# Revit family: RUSHWORK_ 6460
name_source: partatom
category: Арматура трубопроводов
units: mm (PartAtom-declared; Revit-internal decimal feet)

## family parameters
Всегда вертикально = Нет
На основе рабочей плоскости = Нет
Общий = Нет
При загрузке вырезать с полостями = Нет
Размер круглого соединителя = Использовать диаметр
Тип детали = Вставляется

## types (8) — shared parameters
ADSK_Единица измерения = шт
ADSK_Завод-изготовитель = ООО TД "РАШВОРК"
URL = https://rwru.ru
Изготовитель = ООО TД "РАШВОРК"
Корпус = нерж. сталь CF8M
zero-valued in all types: Отметка по умолчанию

## per-type parameters (varying)
| type | ADSK_Код изделия | ADSK_Масса | D1 | D2 | D3 | DN | H | H3 | H4 | H5 | L | L1 | L2 |
| Фильтр сетчатый РАШВОРК 6460-008-40, DN008 PN40, корпус - CF8М, сетка - AISI316, ячейка - 1 мм, ВР/ВР | 6460-008-40 | 0.2 | 26 мм | 24 мм | 27 мм | 10 мм | 43 мм | 25 мм | 21 мм | 7 мм | 64 мм | 10 мм | 16 мм |
| Фильтр сетчатый РАШВОРК 6460-010-40, DN010 PN40, корпус - CF8М, сетка - AISI316, ячейка - 1 мм, ВР/ВР | 6460-010-40 | 0.2 | 26 мм | 24 мм | 24 мм | 12 мм | 43 мм | 25 мм | 21 мм | 7 мм | 64 мм | 10 мм | 16 мм |
| Фильтр сетчатый РАШВОРК 6460-020-40, DN020 PN40, корпус - CF8М, сетка - AISI316, ячейка - 1 мм, ВР/ВР | 6460-020-40 | 0.33 | 32 мм | 29 мм | 29 мм | 20 мм | 50 мм | 32 мм | 21 мм | 7 мм | 80 мм | 16 мм | 15 мм |
| Фильтр сетчатый РАШВОРК 6460-015-40, DN015 PN40, корпус - CF8М, сетка - AISI316, ячейка - 1 мм, ВР/ВР | 6460-015-40 | 0.2 | 26 мм | 24 мм | 24 мм | 15 мм | 43 мм | 25 мм | 21 мм | 7 мм | 64 мм | 10 мм | 16 мм |
| Фильтр сетчатый РАШВОРК 6460-025-40, DN025 PN40, корпус - CF8М, сетка - AISI316, ячейка - 1 мм, ВР/ВР | 6460-025-40 | 0.58 | 40 мм | 34 мм | 45 мм | 25 мм | 65 мм | 43 мм | 25 мм | 9 мм | 90 мм | 16 мм | 16 мм |
| Фильтр сетчатый РАШВОРК 6460-032-40, DN032 PN40, корпус - CF8М, сетка - AISI316, ячейка - 1 мм, ВР/ВР | 6460-032-40 | 0.75 | 48 мм | 45 мм | 47 мм | 32 мм | 69 мм | 47 мм | 25 мм | 10 мм | 106 мм | 20 мм | 16 мм |
| Фильтр сетчатый РАШВОРК 6460-040-40, DN040 PN40, корпус - CF8М, сетка - AISI316, ячейка - 1 мм, ВР/ВР | 6460-040-40 | 1.05 | 55 мм | 51 мм | 55 мм | 40 мм | 79 мм | 53 мм | 27 мм | 11 мм | 119 мм | 22 мм | 16 мм |
| Фильтр сетчатый РАШВОРК 6460-050-40, DN050 PN40, корпус - CF8М, сетка - AISI316, ячейка - 1 мм, ВР/ВР | 6460-050-40 | 1.57 | 68 мм | 65 мм | 67 мм | 50 мм | 92 мм | 66 мм | 29 мм | 12 мм | 140 мм | 22 мм | 29 мм |

note: column(s) folded — value = type name in every type: ADSK_Наименование

## geometry (parser evidence)
native form markers: Blend x21
no freeform markers — native parametric forms only
